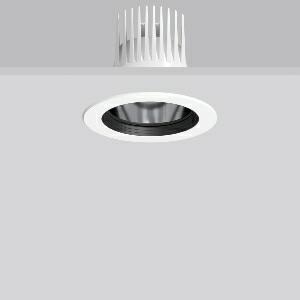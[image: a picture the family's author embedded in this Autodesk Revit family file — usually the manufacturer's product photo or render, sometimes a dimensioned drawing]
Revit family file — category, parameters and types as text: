
# Revit family: heledon_maxi_e_901756_002_3_874e
name_source: partatom
category: Lighting Fixtures
units: mm (PartAtom-declared; Revit-internal decimal feet)

## family parameters
Cut with Voids When Loaded = No
Host = Face
Light Source = No
Part Type = Normal
Room Calculation Point = No
Round Connector Dimension = Use Diameter
Shared = No

## types (1)
- HELEDON maxi E (1 x LED Modul 935, 3300 lm, 3500)
    Apparent Load = 25 VA
    Approval mark = CE
    CIE Flux Codes = 100 100 100 100 100
    Color Rendering = 92
    Color Temperature = 3500
    Default Elevation = 1800 mm
    Description = Series: HELEDON maxi
Round recessed downlight. Housing: die-cast aluminium, powder-coated. Black plastic ring and recessed LED to prevent glare from the side. Optical assembly with reflector made of MIRO-Silver with 98% total light reflection for outstanding efficiency - can be changed without tools. Best colour rendering index Ra>90. Suitable for Recessed ceiling mounting. Installation without tools thanks to spring fastening system. Including separate LED converter with connecting cable 600 mm.High quality converter without flickering and stroboscopic effect. Through-wiring box (5 pole) available as accessory. The following accessories can be mounted without use of tools: interchangeable lenses, decorative glasses, honeycomb louvre, clear and frosted diffusers, white interchangeable plastic ring. 
Colour: traffic white, matt (RAL 9016)
Diameter: 162 mm
Height: 3 mm
Cut-out diameter: 152 mm
Recess height: 200 mm
Luminaire: recess height: 135 mm
Lamp: LED
Socket: without socket
Colour temperature: 3500K
Colour rendering index (CRI): 92
System power: 25 W
Rated luminous flux: 3300 lm
Luminous efficiency: 132 lm/W
Control gear: Regulated power supply
Protection class: II
Type of protection: IP 20
    Height = 0 mm  [stored 0 ft]
    Lamp = 1 x LED Modul 935
    Lamp Light Flux = 3300 lm
    Lamp count = 1
    Length = 162 mm
    Lifetime = 50000 h
    Luminous efficacy = 132 lm/W
    Manufacturer = RZB
    ModVariant = No
    Model = 901756.002.3
    Mounting Place = Ceiling
    Mounting Type = Recessed
    Number of Poles = 1
    OnlyDefault = Yes
    Power Factor = 1
    Product Name = HELEDON maxi E
    Product group = Recessed downlights
    ProductGroupID = 402
    Protection Class = Protection class II
    Protection Degree = IP 20
    RLX_Detail_Level = 1
    RLX_Emergency_Light_Flux = 0 lm
    RLX_Emergency_Type = 0
    RLX_Emergency_Type_DB = No
    RlxData = <blob elided: 119093 chars, md5=c2dcb189>
    Socket = socket
    Standby Power = 0 W
    System Light Flux = 3300 lm
    System Power = 25 W
    Type Comments = Product without accessories
    Type Image = 901662.002.jpg
    URL = http://relux.com
    VarID = ---
    Voltage = 230 V
    Voltage Range = 220-240 V
    Weight = 0.00 kg
    Width = 0 mm  [stored 0 ft]

note: [stored X ft] marks values corroborated as IEEE doubles in the binary element streams (Revit-internal decimal feet)

## geometry (parser evidence)
native form markers: Blend x4, Sweep x14
no freeform markers — native parametric forms only
